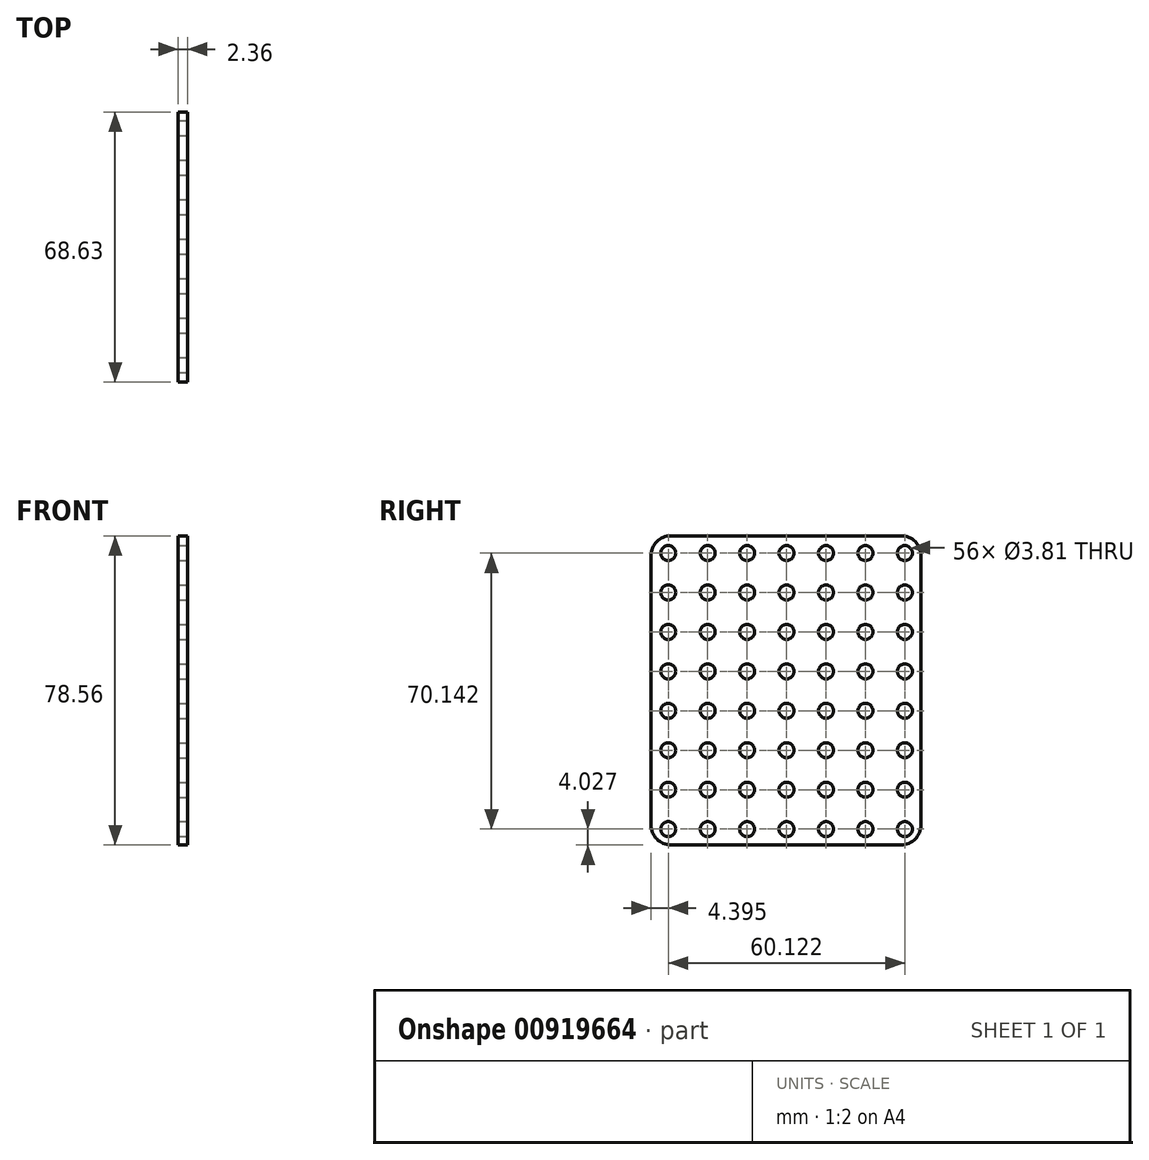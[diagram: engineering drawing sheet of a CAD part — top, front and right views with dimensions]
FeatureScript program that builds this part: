
annotation { "Feature Type Name" : "Feature", "Feature Type Description" : "" }
export const myFeature = defineFeature(function(context is Context, id is Id, definition is map)
    precondition{}
    {
        {
            var Q0;
            Q0=qCreatedBy(makeId("Right.planeOp"),FACE);
            var sketch = newSketch(context, id + "F0", { "sketchPlane" : qUnion([Q0])});
            skLineSegment(sketch, "E0.bottom", {"start": v(-35.18, 37.4) * mm, "end": v(33.45, 37.4) * mm});
            skLineSegment(sketch, "E0.top", {"start": v(-35.18, -41.16) * mm, "end": v(33.45, -41.16) * mm});
            skLineSegment(sketch, "E0.left", {"start": v(-35.18, 37.4) * mm, "end": v(-35.18, -41.16) * mm});
            skLineSegment(sketch, "E0.right", {"start": v(33.45, 37.4) * mm, "end": v(33.45, -41.16) * mm});
            skSolve(sketch);
        }
        {
            var Q0;
            Q0=makeQuery(id+"F0.imprint","IMPRINT",FACE,{"disambiguationData":[TD([[makeQuery(id+"F0.imprint","IMPRINT",EDGE,{"derivedFrom":sQuery(id+"F0.wireOp",EDGE,"E0.bottom")}),-1.0]])]});
            extrude(context, id + "F1", {"entities" : qUnion([Q0]), "depth" : 2.36 * mm, "offsetDistance" : 25.4 * mm});
        }
        {
            var Q0;
            Q0=makeQuery(id+"F1.opExtrude","SWEPT_EDGE",EDGE,{"disambiguationData":[OSD([sQuery(id+"F0.wireOp",EDGE,"E0.top"),sQuery(id+"F0.wireOp",EDGE,"E0.left")])]});
            var Q1;
            Q1=makeQuery(id+"F1.opExtrude","SWEPT_EDGE",EDGE,{"disambiguationData":[OSD([sQuery(id+"F0.wireOp",EDGE,"E0.top"),sQuery(id+"F0.wireOp",EDGE,"E0.right")])]});
            var Q2;
            Q2=makeQuery(id+"F1.opExtrude","SWEPT_EDGE",EDGE,{"disambiguationData":[OSD([sQuery(id+"F0.wireOp",EDGE,"E0.bottom"),sQuery(id+"F0.wireOp",EDGE,"E0.right")])]});
            var Q3;
            Q3=makeQuery(id+"F1.opExtrude","SWEPT_EDGE",EDGE,{"disambiguationData":[OSD([sQuery(id+"F0.wireOp",EDGE,"E0.bottom"),sQuery(id+"F0.wireOp",EDGE,"E0.left")])]});
            fillet(context, id + "F2", {"entities" : qUnion([Q0, Q1, Q2, Q3]), "radius" : 5.08 * mm, "tangentPropagation" : true, "allowEdgeOverflow" : false});
        }
        {
            var Q0;
            Q0=makeQuery(id+"F1.opExtrude","CAP_FACE",FACE,{"disambiguationData":[OSD([sQuery(id+"F0.wireOp",EDGE,"E0.bottom"),sQuery(id+"F0.wireOp",EDGE,"E0.top"),sQuery(id+"F0.wireOp",EDGE,"E0.left"),sQuery(id+"F0.wireOp",EDGE,"E0.right")])],"isStart":false});
            var sketch = newSketch(context, id + "F3", { "sketchPlane" : qUnion([Q0])});
            skCircle(sketch, "E1", {"center": v(-30.78, 33) * mm, "radius": 1.9 * mm});
            skCircle(sketch, "E2.1.0.0", {"center": v(-20.76, 33) * mm, "radius": 1.9 * mm});
            skCircle(sketch, "E2.2.0.0", {"center": v(-10.74, 33) * mm, "radius": 1.9 * mm});
            skCircle(sketch, "E2.3.0.0", {"center": v(-0.72, 33) * mm, "radius": 1.9 * mm});
            skCircle(sketch, "E2.4.0.0", {"center": v(9.3, 33) * mm, "radius": 1.9 * mm});
            skCircle(sketch, "E2.5.0.0", {"center": v(19.32, 33) * mm, "radius": 1.9 * mm});
            skCircle(sketch, "E2.6.0.0", {"center": v(29.34, 33) * mm, "radius": 1.9 * mm});
            skLineSegment(sketch, "E2.direction1", {"start": v(-30.78, 33) * mm, "end": v(-20.76, 33) * mm, "construction": true});
            skCircle(sketch, "E3.0.1.0", {"center": v(-30.78, 22.99) * mm, "radius": 1.9 * mm});
            skCircle(sketch, "E3.0.1.1", {"center": v(-20.76, 22.99) * mm, "radius": 1.9 * mm});
            skCircle(sketch, "E3.0.1.2", {"center": v(-10.74, 22.99) * mm, "radius": 1.9 * mm});
            skCircle(sketch, "E3.0.1.3", {"center": v(-0.72, 22.99) * mm, "radius": 1.9 * mm});
            skCircle(sketch, "E3.0.1.4", {"center": v(9.3, 22.99) * mm, "radius": 1.9 * mm});
            skCircle(sketch, "E3.0.1.5", {"center": v(19.32, 22.99) * mm, "radius": 1.9 * mm});
            skCircle(sketch, "E3.0.1.6", {"center": v(29.34, 22.99) * mm, "radius": 1.9 * mm});
            skCircle(sketch, "E3.0.2.0", {"center": v(-30.78, 12.97) * mm, "radius": 1.9 * mm});
            skCircle(sketch, "E3.0.2.1", {"center": v(-20.76, 12.97) * mm, "radius": 1.9 * mm});
            skCircle(sketch, "E3.0.2.2", {"center": v(-10.74, 12.97) * mm, "radius": 1.9 * mm});
            skCircle(sketch, "E3.0.2.3", {"center": v(-0.72, 12.97) * mm, "radius": 1.9 * mm});
            skCircle(sketch, "E3.0.2.4", {"center": v(9.3, 12.97) * mm, "radius": 1.9 * mm});
            skCircle(sketch, "E3.0.2.5", {"center": v(19.32, 12.97) * mm, "radius": 1.9 * mm});
            skCircle(sketch, "E3.0.2.6", {"center": v(29.34, 12.97) * mm, "radius": 1.9 * mm});
            skCircle(sketch, "E3.0.3.0", {"center": v(-30.78, 2.95) * mm, "radius": 1.9 * mm});
            skCircle(sketch, "E3.0.3.1", {"center": v(-20.76, 2.95) * mm, "radius": 1.9 * mm});
            skCircle(sketch, "E3.0.3.2", {"center": v(-10.74, 2.95) * mm, "radius": 1.9 * mm});
            skCircle(sketch, "E3.0.3.3", {"center": v(-0.72, 2.95) * mm, "radius": 1.9 * mm});
            skCircle(sketch, "E3.0.3.4", {"center": v(9.3, 2.95) * mm, "radius": 1.9 * mm});
            skCircle(sketch, "E3.0.3.5", {"center": v(19.32, 2.95) * mm, "radius": 1.9 * mm});
            skCircle(sketch, "E3.0.3.6", {"center": v(29.34, 2.95) * mm, "radius": 1.9 * mm});
            skCircle(sketch, "E3.0.4.0", {"center": v(-30.78, -7.07) * mm, "radius": 1.9 * mm});
            skCircle(sketch, "E3.0.4.1", {"center": v(-20.76, -7.07) * mm, "radius": 1.9 * mm});
            skCircle(sketch, "E3.0.4.2", {"center": v(-10.74, -7.07) * mm, "radius": 1.9 * mm});
            skCircle(sketch, "E3.0.4.3", {"center": v(-0.72, -7.07) * mm, "radius": 1.9 * mm});
            skCircle(sketch, "E3.0.4.4", {"center": v(9.3, -7.07) * mm, "radius": 1.9 * mm});
            skCircle(sketch, "E3.0.4.5", {"center": v(19.32, -7.07) * mm, "radius": 1.9 * mm});
            skCircle(sketch, "E3.0.4.6", {"center": v(29.34, -7.07) * mm, "radius": 1.9 * mm});
            skCircle(sketch, "E3.0.5.0", {"center": v(-30.78, -17.1) * mm, "radius": 1.9 * mm});
            skCircle(sketch, "E3.0.5.1", {"center": v(-20.76, -17.1) * mm, "radius": 1.9 * mm});
            skCircle(sketch, "E3.0.5.2", {"center": v(-10.74, -17.1) * mm, "radius": 1.9 * mm});
            skCircle(sketch, "E3.0.5.3", {"center": v(-0.72, -17.1) * mm, "radius": 1.9 * mm});
            skCircle(sketch, "E3.0.5.4", {"center": v(9.3, -17.1) * mm, "radius": 1.9 * mm});
            skCircle(sketch, "E3.0.5.5", {"center": v(19.32, -17.1) * mm, "radius": 1.9 * mm});
            skCircle(sketch, "E3.0.5.6", {"center": v(29.34, -17.1) * mm, "radius": 1.9 * mm});
            skCircle(sketch, "E3.0.6.0", {"center": v(-30.78, -27.11) * mm, "radius": 1.9 * mm});
            skCircle(sketch, "E3.0.6.1", {"center": v(-20.76, -27.11) * mm, "radius": 1.9 * mm});
            skCircle(sketch, "E3.0.6.2", {"center": v(-10.74, -27.11) * mm, "radius": 1.9 * mm});
            skCircle(sketch, "E3.0.6.3", {"center": v(-0.72, -27.11) * mm, "radius": 1.9 * mm});
            skCircle(sketch, "E3.0.6.4", {"center": v(9.3, -27.11) * mm, "radius": 1.9 * mm});
            skCircle(sketch, "E3.0.6.5", {"center": v(19.32, -27.11) * mm, "radius": 1.9 * mm});
            skCircle(sketch, "E3.0.6.6", {"center": v(29.34, -27.11) * mm, "radius": 1.9 * mm});
            skCircle(sketch, "E3.0.7.0", {"center": v(-30.78, -37.13) * mm, "radius": 1.9 * mm});
            skCircle(sketch, "E3.0.7.1", {"center": v(-20.76, -37.13) * mm, "radius": 1.9 * mm});
            skCircle(sketch, "E3.0.7.2", {"center": v(-10.74, -37.13) * mm, "radius": 1.9 * mm});
            skCircle(sketch, "E3.0.7.3", {"center": v(-0.72, -37.13) * mm, "radius": 1.9 * mm});
            skCircle(sketch, "E3.0.7.4", {"center": v(9.3, -37.13) * mm, "radius": 1.9 * mm});
            skCircle(sketch, "E3.0.7.5", {"center": v(19.32, -37.13) * mm, "radius": 1.9 * mm});
            skCircle(sketch, "E3.0.7.6", {"center": v(29.34, -37.13) * mm, "radius": 1.9 * mm});
            skLineSegment(sketch, "E3.direction1", {"start": v(-30.78, 33) * mm, "end": v(12.65, 33) * mm, "construction": true});
            skLineSegment(sketch, "E3.direction2", {"start": v(-30.78, 33) * mm, "end": v(-30.78, 22.99) * mm, "construction": true});
            skSolve(sketch);
        }
        {
            var Q0;
            Q0=makeQuery(id+"F3.imprint","IMPRINT",FACE,{"disambiguationData":[TD([[makeQuery(id+"F3.imprint","IMPRINT",EDGE,{"derivedFrom":sQuery(id+"F3.wireOp",EDGE,"E1")}),1.0]])]});
            var Q1;
            Q1=makeQuery(id+"F3.imprint","IMPRINT",FACE,{"disambiguationData":[TD([[makeQuery(id+"F3.imprint","IMPRINT",EDGE,{"derivedFrom":sQuery(id+"F3.wireOp",EDGE,"E2.1.0.0")}),1.0]])]});
            var Q2;
            Q2=makeQuery(id+"F3.imprint","IMPRINT",FACE,{"disambiguationData":[TD([[makeQuery(id+"F3.imprint","IMPRINT",EDGE,{"derivedFrom":sQuery(id+"F3.wireOp",EDGE,"E2.2.0.0")}),1.0]])]});
            var Q3;
            Q3=makeQuery(id+"F3.imprint","IMPRINT",FACE,{"disambiguationData":[TD([[makeQuery(id+"F3.imprint","IMPRINT",EDGE,{"derivedFrom":sQuery(id+"F3.wireOp",EDGE,"E2.3.0.0")}),1.0]])]});
            var Q4;
            Q4=makeQuery(id+"F3.imprint","IMPRINT",FACE,{"disambiguationData":[TD([[makeQuery(id+"F3.imprint","IMPRINT",EDGE,{"derivedFrom":sQuery(id+"F3.wireOp",EDGE,"E2.4.0.0")}),1.0]])]});
            var Q5;
            Q5=makeQuery(id+"F3.imprint","IMPRINT",FACE,{"disambiguationData":[TD([[makeQuery(id+"F3.imprint","IMPRINT",EDGE,{"derivedFrom":sQuery(id+"F3.wireOp",EDGE,"E2.5.0.0")}),1.0]])]});
            var Q6;
            Q6=makeQuery(id+"F3.imprint","IMPRINT",FACE,{"disambiguationData":[TD([[makeQuery(id+"F3.imprint","IMPRINT",EDGE,{"derivedFrom":sQuery(id+"F3.wireOp",EDGE,"E2.6.0.0")}),1.0]])]});
            var Q7;
            Q7=makeQuery(id+"F3.imprint","IMPRINT",FACE,{"disambiguationData":[TD([[makeQuery(id+"F3.imprint","IMPRINT",EDGE,{"derivedFrom":sQuery(id+"F3.wireOp",EDGE,"E3.0.1.6")}),1.0]])]});
            var Q8;
            Q8=makeQuery(id+"F3.imprint","IMPRINT",FACE,{"disambiguationData":[TD([[makeQuery(id+"F3.imprint","IMPRINT",EDGE,{"derivedFrom":sQuery(id+"F3.wireOp",EDGE,"E3.0.1.5")}),1.0]])]});
            var Q9;
            Q9=makeQuery(id+"F3.imprint","IMPRINT",FACE,{"disambiguationData":[TD([[makeQuery(id+"F3.imprint","IMPRINT",EDGE,{"derivedFrom":sQuery(id+"F3.wireOp",EDGE,"E3.0.1.4")}),1.0]])]});
            var Q10;
            Q10=makeQuery(id+"F3.imprint","IMPRINT",FACE,{"disambiguationData":[TD([[makeQuery(id+"F3.imprint","IMPRINT",EDGE,{"derivedFrom":sQuery(id+"F3.wireOp",EDGE,"E3.0.1.3")}),1.0]])]});
            var Q11;
            Q11=makeQuery(id+"F3.imprint","IMPRINT",FACE,{"disambiguationData":[TD([[makeQuery(id+"F3.imprint","IMPRINT",EDGE,{"derivedFrom":sQuery(id+"F3.wireOp",EDGE,"E3.0.1.2")}),1.0]])]});
            var Q12;
            Q12=makeQuery(id+"F3.imprint","IMPRINT",FACE,{"disambiguationData":[TD([[makeQuery(id+"F3.imprint","IMPRINT",EDGE,{"derivedFrom":sQuery(id+"F3.wireOp",EDGE,"E3.0.1.1")}),1.0]])]});
            var Q13;
            Q13=makeQuery(id+"F3.imprint","IMPRINT",FACE,{"disambiguationData":[TD([[makeQuery(id+"F3.imprint","IMPRINT",EDGE,{"derivedFrom":sQuery(id+"F3.wireOp",EDGE,"E3.0.1.0")}),1.0]])]});
            var Q14;
            Q14=makeQuery(id+"F3.imprint","IMPRINT",FACE,{"disambiguationData":[TD([[makeQuery(id+"F3.imprint","IMPRINT",EDGE,{"derivedFrom":sQuery(id+"F3.wireOp",EDGE,"E3.0.2.0")}),1.0]])]});
            var Q15;
            Q15=makeQuery(id+"F3.imprint","IMPRINT",FACE,{"disambiguationData":[TD([[makeQuery(id+"F3.imprint","IMPRINT",EDGE,{"derivedFrom":sQuery(id+"F3.wireOp",EDGE,"E3.0.2.1")}),1.0]])]});
            var Q16;
            Q16=makeQuery(id+"F3.imprint","IMPRINT",FACE,{"disambiguationData":[TD([[makeQuery(id+"F3.imprint","IMPRINT",EDGE,{"derivedFrom":sQuery(id+"F3.wireOp",EDGE,"E3.0.2.2")}),1.0]])]});
            var Q17;
            Q17=makeQuery(id+"F3.imprint","IMPRINT",FACE,{"disambiguationData":[TD([[makeQuery(id+"F3.imprint","IMPRINT",EDGE,{"derivedFrom":sQuery(id+"F3.wireOp",EDGE,"E3.0.2.3")}),1.0]])]});
            var Q18;
            Q18=makeQuery(id+"F3.imprint","IMPRINT",FACE,{"disambiguationData":[TD([[makeQuery(id+"F3.imprint","IMPRINT",EDGE,{"derivedFrom":sQuery(id+"F3.wireOp",EDGE,"E3.0.2.4")}),1.0]])]});
            var Q19;
            Q19=makeQuery(id+"F3.imprint","IMPRINT",FACE,{"disambiguationData":[TD([[makeQuery(id+"F3.imprint","IMPRINT",EDGE,{"derivedFrom":sQuery(id+"F3.wireOp",EDGE,"E3.0.2.5")}),1.0]])]});
            var Q20;
            Q20=makeQuery(id+"F3.imprint","IMPRINT",FACE,{"disambiguationData":[TD([[makeQuery(id+"F3.imprint","IMPRINT",EDGE,{"derivedFrom":sQuery(id+"F3.wireOp",EDGE,"E3.0.2.6")}),1.0]])]});
            var Q21;
            Q21=makeQuery(id+"F3.imprint","IMPRINT",FACE,{"disambiguationData":[TD([[makeQuery(id+"F3.imprint","IMPRINT",EDGE,{"derivedFrom":sQuery(id+"F3.wireOp",EDGE,"E3.0.3.0")}),1.0]])]});
            var Q22;
            Q22=makeQuery(id+"F3.imprint","IMPRINT",FACE,{"disambiguationData":[TD([[makeQuery(id+"F3.imprint","IMPRINT",EDGE,{"derivedFrom":sQuery(id+"F3.wireOp",EDGE,"E3.0.3.1")}),1.0]])]});
            var Q23;
            Q23=makeQuery(id+"F3.imprint","IMPRINT",FACE,{"disambiguationData":[TD([[makeQuery(id+"F3.imprint","IMPRINT",EDGE,{"derivedFrom":sQuery(id+"F3.wireOp",EDGE,"E3.0.3.2")}),1.0]])]});
            var Q24;
            Q24=makeQuery(id+"F3.imprint","IMPRINT",FACE,{"disambiguationData":[TD([[makeQuery(id+"F3.imprint","IMPRINT",EDGE,{"derivedFrom":sQuery(id+"F3.wireOp",EDGE,"E3.0.3.3")}),1.0]])]});
            var Q25;
            Q25=makeQuery(id+"F3.imprint","IMPRINT",FACE,{"disambiguationData":[TD([[makeQuery(id+"F3.imprint","IMPRINT",EDGE,{"derivedFrom":sQuery(id+"F3.wireOp",EDGE,"E3.0.3.4")}),1.0]])]});
            var Q26;
            Q26=makeQuery(id+"F3.imprint","IMPRINT",FACE,{"disambiguationData":[TD([[makeQuery(id+"F3.imprint","IMPRINT",EDGE,{"derivedFrom":sQuery(id+"F3.wireOp",EDGE,"E3.0.3.5")}),1.0]])]});
            var Q27;
            Q27=makeQuery(id+"F3.imprint","IMPRINT",FACE,{"disambiguationData":[TD([[makeQuery(id+"F3.imprint","IMPRINT",EDGE,{"derivedFrom":sQuery(id+"F3.wireOp",EDGE,"E3.0.3.6")}),1.0]])]});
            var Q28;
            Q28=makeQuery(id+"F3.imprint","IMPRINT",FACE,{"disambiguationData":[TD([[makeQuery(id+"F3.imprint","IMPRINT",EDGE,{"derivedFrom":sQuery(id+"F3.wireOp",EDGE,"E3.0.4.0")}),1.0]])]});
            var Q29;
            Q29=makeQuery(id+"F3.imprint","IMPRINT",FACE,{"disambiguationData":[TD([[makeQuery(id+"F3.imprint","IMPRINT",EDGE,{"derivedFrom":sQuery(id+"F3.wireOp",EDGE,"E3.0.4.1")}),1.0]])]});
            var Q30;
            Q30=makeQuery(id+"F3.imprint","IMPRINT",FACE,{"disambiguationData":[TD([[makeQuery(id+"F3.imprint","IMPRINT",EDGE,{"derivedFrom":sQuery(id+"F3.wireOp",EDGE,"E3.0.4.2")}),1.0]])]});
            var Q31;
            Q31=makeQuery(id+"F3.imprint","IMPRINT",FACE,{"disambiguationData":[TD([[makeQuery(id+"F3.imprint","IMPRINT",EDGE,{"derivedFrom":sQuery(id+"F3.wireOp",EDGE,"E3.0.4.3")}),1.0]])]});
            var Q32;
            Q32=makeQuery(id+"F3.imprint","IMPRINT",FACE,{"disambiguationData":[TD([[makeQuery(id+"F3.imprint","IMPRINT",EDGE,{"derivedFrom":sQuery(id+"F3.wireOp",EDGE,"E3.0.4.4")}),1.0]])]});
            var Q33;
            Q33=makeQuery(id+"F3.imprint","IMPRINT",FACE,{"disambiguationData":[TD([[makeQuery(id+"F3.imprint","IMPRINT",EDGE,{"derivedFrom":sQuery(id+"F3.wireOp",EDGE,"E3.0.4.5")}),1.0]])]});
            var Q34;
            Q34=makeQuery(id+"F3.imprint","IMPRINT",FACE,{"disambiguationData":[TD([[makeQuery(id+"F3.imprint","IMPRINT",EDGE,{"derivedFrom":sQuery(id+"F3.wireOp",EDGE,"E3.0.4.6")}),1.0]])]});
            var Q35;
            Q35=makeQuery(id+"F3.imprint","IMPRINT",FACE,{"disambiguationData":[TD([[makeQuery(id+"F3.imprint","IMPRINT",EDGE,{"derivedFrom":sQuery(id+"F3.wireOp",EDGE,"E3.0.5.0")}),1.0]])]});
            var Q36;
            Q36=makeQuery(id+"F3.imprint","IMPRINT",FACE,{"disambiguationData":[TD([[makeQuery(id+"F3.imprint","IMPRINT",EDGE,{"derivedFrom":sQuery(id+"F3.wireOp",EDGE,"E3.0.5.1")}),1.0]])]});
            var Q37;
            Q37=makeQuery(id+"F3.imprint","IMPRINT",FACE,{"disambiguationData":[TD([[makeQuery(id+"F3.imprint","IMPRINT",EDGE,{"derivedFrom":sQuery(id+"F3.wireOp",EDGE,"E3.0.5.2")}),1.0]])]});
            var Q38;
            Q38=makeQuery(id+"F3.imprint","IMPRINT",FACE,{"disambiguationData":[TD([[makeQuery(id+"F3.imprint","IMPRINT",EDGE,{"derivedFrom":sQuery(id+"F3.wireOp",EDGE,"E3.0.5.3")}),1.0]])]});
            var Q39;
            Q39=makeQuery(id+"F3.imprint","IMPRINT",FACE,{"disambiguationData":[TD([[makeQuery(id+"F3.imprint","IMPRINT",EDGE,{"derivedFrom":sQuery(id+"F3.wireOp",EDGE,"E3.0.5.4")}),1.0]])]});
            var Q40;
            Q40=makeQuery(id+"F3.imprint","IMPRINT",FACE,{"disambiguationData":[TD([[makeQuery(id+"F3.imprint","IMPRINT",EDGE,{"derivedFrom":sQuery(id+"F3.wireOp",EDGE,"E3.0.5.5")}),1.0]])]});
            var Q41;
            Q41=makeQuery(id+"F3.imprint","IMPRINT",FACE,{"disambiguationData":[TD([[makeQuery(id+"F3.imprint","IMPRINT",EDGE,{"derivedFrom":sQuery(id+"F3.wireOp",EDGE,"E3.0.5.6")}),1.0]])]});
            var Q42;
            Q42=makeQuery(id+"F3.imprint","IMPRINT",FACE,{"disambiguationData":[TD([[makeQuery(id+"F3.imprint","IMPRINT",EDGE,{"derivedFrom":sQuery(id+"F3.wireOp",EDGE,"E3.0.6.0")}),1.0]])]});
            var Q43;
            Q43=makeQuery(id+"F3.imprint","IMPRINT",FACE,{"disambiguationData":[TD([[makeQuery(id+"F3.imprint","IMPRINT",EDGE,{"derivedFrom":sQuery(id+"F3.wireOp",EDGE,"E3.0.6.1")}),1.0]])]});
            var Q44;
            Q44=makeQuery(id+"F3.imprint","IMPRINT",FACE,{"disambiguationData":[TD([[makeQuery(id+"F3.imprint","IMPRINT",EDGE,{"derivedFrom":sQuery(id+"F3.wireOp",EDGE,"E3.0.6.2")}),1.0]])]});
            var Q45;
            Q45=makeQuery(id+"F3.imprint","IMPRINT",FACE,{"disambiguationData":[TD([[makeQuery(id+"F3.imprint","IMPRINT",EDGE,{"derivedFrom":sQuery(id+"F3.wireOp",EDGE,"E3.0.6.3")}),1.0]])]});
            var Q46;
            Q46=makeQuery(id+"F3.imprint","IMPRINT",FACE,{"disambiguationData":[TD([[makeQuery(id+"F3.imprint","IMPRINT",EDGE,{"derivedFrom":sQuery(id+"F3.wireOp",EDGE,"E3.0.6.4")}),1.0]])]});
            var Q47;
            Q47=makeQuery(id+"F3.imprint","IMPRINT",FACE,{"disambiguationData":[TD([[makeQuery(id+"F3.imprint","IMPRINT",EDGE,{"derivedFrom":sQuery(id+"F3.wireOp",EDGE,"E3.0.6.5")}),1.0]])]});
            var Q48;
            Q48=makeQuery(id+"F3.imprint","IMPRINT",FACE,{"disambiguationData":[TD([[makeQuery(id+"F3.imprint","IMPRINT",EDGE,{"derivedFrom":sQuery(id+"F3.wireOp",EDGE,"E3.0.6.6")}),1.0]])]});
            var Q49;
            Q49=makeQuery(id+"F3.imprint","IMPRINT",FACE,{"disambiguationData":[TD([[makeQuery(id+"F3.imprint","IMPRINT",EDGE,{"derivedFrom":sQuery(id+"F3.wireOp",EDGE,"E3.0.7.0")}),1.0]])]});
            var Q50;
            Q50=makeQuery(id+"F3.imprint","IMPRINT",FACE,{"disambiguationData":[TD([[makeQuery(id+"F3.imprint","IMPRINT",EDGE,{"derivedFrom":sQuery(id+"F3.wireOp",EDGE,"E3.0.7.1")}),1.0]])]});
            var Q51;
            Q51=makeQuery(id+"F3.imprint","IMPRINT",FACE,{"disambiguationData":[TD([[makeQuery(id+"F3.imprint","IMPRINT",EDGE,{"derivedFrom":sQuery(id+"F3.wireOp",EDGE,"E3.0.7.2")}),1.0]])]});
            var Q52;
            Q52=makeQuery(id+"F3.imprint","IMPRINT",FACE,{"disambiguationData":[TD([[makeQuery(id+"F3.imprint","IMPRINT",EDGE,{"derivedFrom":sQuery(id+"F3.wireOp",EDGE,"E3.0.7.3")}),1.0]])]});
            var Q53;
            Q53=makeQuery(id+"F3.imprint","IMPRINT",FACE,{"disambiguationData":[TD([[makeQuery(id+"F3.imprint","IMPRINT",EDGE,{"derivedFrom":sQuery(id+"F3.wireOp",EDGE,"E3.0.7.4")}),1.0]])]});
            var Q54;
            Q54=makeQuery(id+"F3.imprint","IMPRINT",FACE,{"disambiguationData":[TD([[makeQuery(id+"F3.imprint","IMPRINT",EDGE,{"derivedFrom":sQuery(id+"F3.wireOp",EDGE,"E3.0.7.5")}),1.0]])]});
            var Q55;
            Q55=makeQuery(id+"F3.imprint","IMPRINT",FACE,{"disambiguationData":[TD([[makeQuery(id+"F3.imprint","IMPRINT",EDGE,{"derivedFrom":sQuery(id+"F3.wireOp",EDGE,"E3.0.7.6")}),1.0]])]});
            extrude(context, id + "F4", {"entities" : qUnion([Q0, Q1, Q2, Q3, Q4, Q5, Q6, Q7, Q8, Q9, Q10, Q11, Q12, Q13, Q14, Q15, Q16, Q17, Q18, Q19, Q20, Q21, Q22, Q23, Q24, Q25, Q26, Q27, Q28, Q29, Q30, Q31, Q32, Q33, Q34, Q35, Q36, Q37, Q38, Q39, Q40, Q41, Q42, Q43, Q44, Q45, Q46, Q47, Q48, Q49, Q50, Q51, Q52, Q53, Q54, Q55]), "operationType" : NewBodyOperationType.REMOVE, "oppositeDirection" : true, "depth" : 25.4 * mm, "offsetDistance" : 25.4 * mm});
        }
    });
